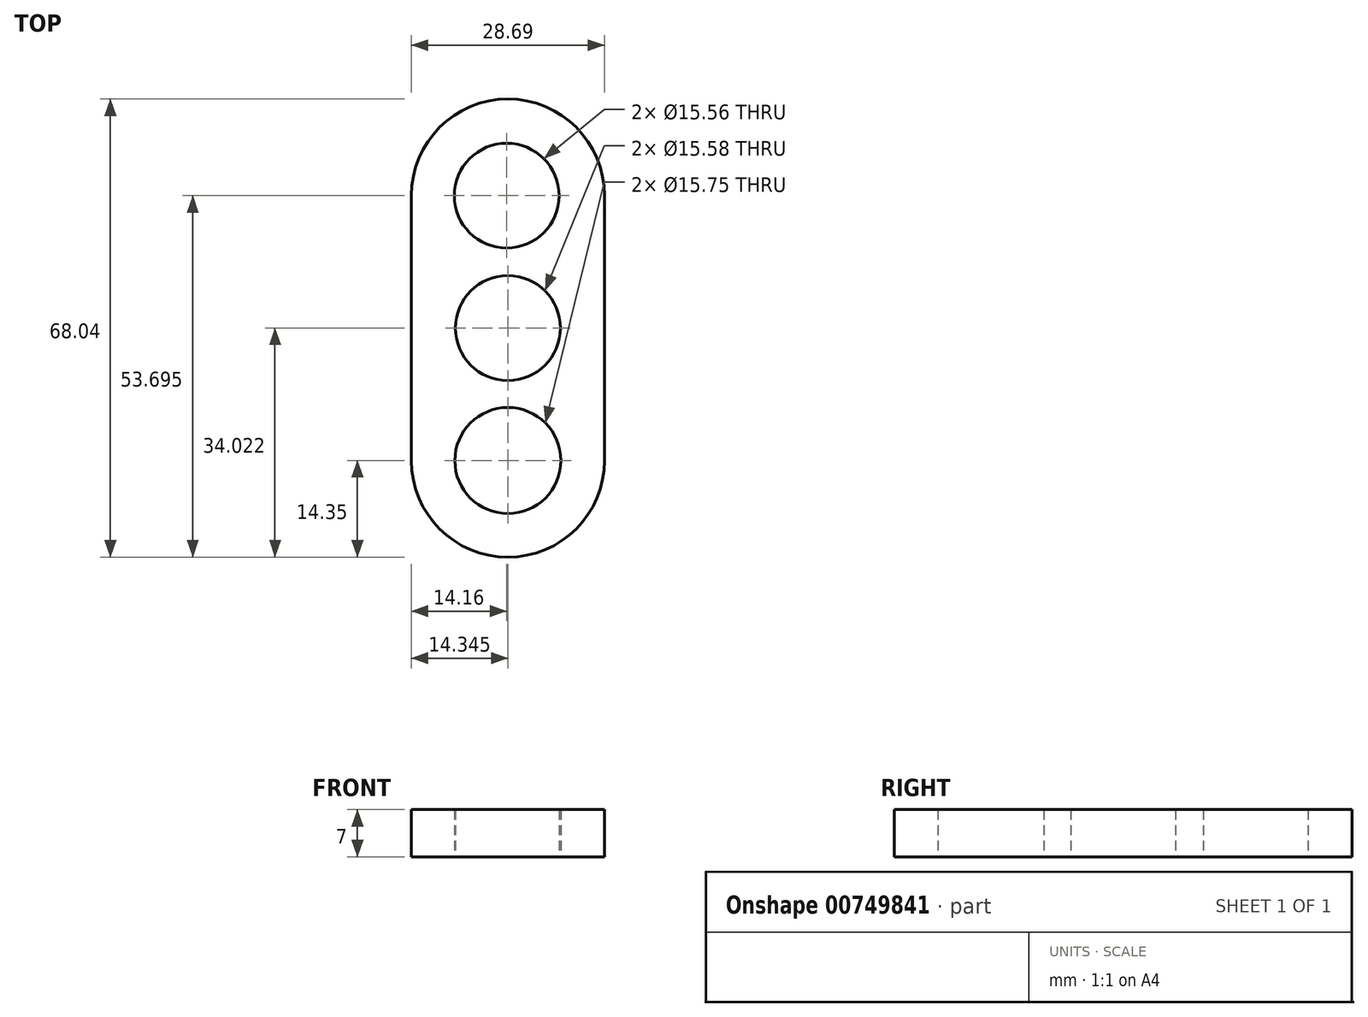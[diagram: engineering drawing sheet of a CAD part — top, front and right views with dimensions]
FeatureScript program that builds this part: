
annotation { "Feature Type Name" : "Feature", "Feature Type Description" : "" }
export const myFeature = defineFeature(function(context is Context, id is Id, definition is map)
    precondition{}
    {
        {
            var Q0;
            Q0=qCreatedBy(makeId("Top.planeOp"),FACE);
            var sketch = newSketch(context, id + "F0", { "sketchPlane" : qUnion([Q0])});
            skCircle(sketch, "E0", {"center": v(-19.84, 39.34) * mm, "radius": 7.78 * mm});
            skArc(sketch, "E1", {"start": v(-5.3, 39.34) * mm, "mid": v(-19.66, 53.7) * mm, "end": v(-34, 39.34) * mm});
            skLineSegment(sketch, "E2", {"start": v(-34, 39.34) * mm, "end": v(-34, 0) * mm});
            skLineSegment(sketch, "E3", {"start": v(-5.3, 39.34) * mm, "end": v(-5.3, 0) * mm});
            skArc(sketch, "E4", {"start": v(-34, 0) * mm, "mid": v(-19.66, -14.35) * mm, "end": v(-5.3, 0) * mm});
            skCircle(sketch, "E5", {"center": v(-19.66, 0) * mm, "radius": 7.88 * mm});
            skLineSegment(sketch, "E6", {"start": v(-5.3, 39.34) * mm, "end": v(-34, 0) * mm});
            skLineSegment(sketch, "E7", {"start": v(-34, 39.34) * mm, "end": v(-5.3, 0) * mm});
            skCircle(sketch, "E8", {"center": v(-19.66, 19.67) * mm, "radius": 7.79 * mm});
            skSolve(sketch);
        }
        {
            var Q0;
            {var subQ0=sQuery(id+"F0.wireOp",EDGE,"E2");Q0=makeQuery(id+"F0.imprint","IMPRINT",FACE,{"disambiguationData":[TD([[makeQuery(id+"F0.imprint","IMPRINT",EDGE,{"derivedFrom":subQ0}),1.0]])]});}
            var Q1;
            {var subQ0=sQuery(id+"F0.wireOp",EDGE,"E3");Q1=makeQuery(id+"F0.imprint","IMPRINT",FACE,{"disambiguationData":[TD([[makeQuery(id+"F0.imprint","IMPRINT",EDGE,{"derivedFrom":subQ0}),-1.0]])]});}
            var Q2;
            Q2=makeQuery(id+"F0.imprint","IMPRINT",FACE,{"disambiguationData":[TD([[makeQuery(id+"F0.imprint","IMPRINT",EDGE,{"derivedFrom":sQuery(id+"F0.wireOp",EDGE,"E0")}),-1.0]])]});
            var Q3;
            {var subQ1=sQuery(id+"F0.wireOp",EDGE,"E4");Q3=makeQuery(id+"F0.imprint","IMPRINT",FACE,{"disambiguationData":[TD([[makeQuery(id+"F0.imprint","IMPRINT",EDGE,{"derivedFrom":subQ1}),1.0]])]});}
            extrude(context, id + "F1", {"entities" : qUnion([Q0, Q1, Q2, Q3]), "depth" : 7 * mm, "offsetDistance" : 25.4 * mm});
        }
    });
